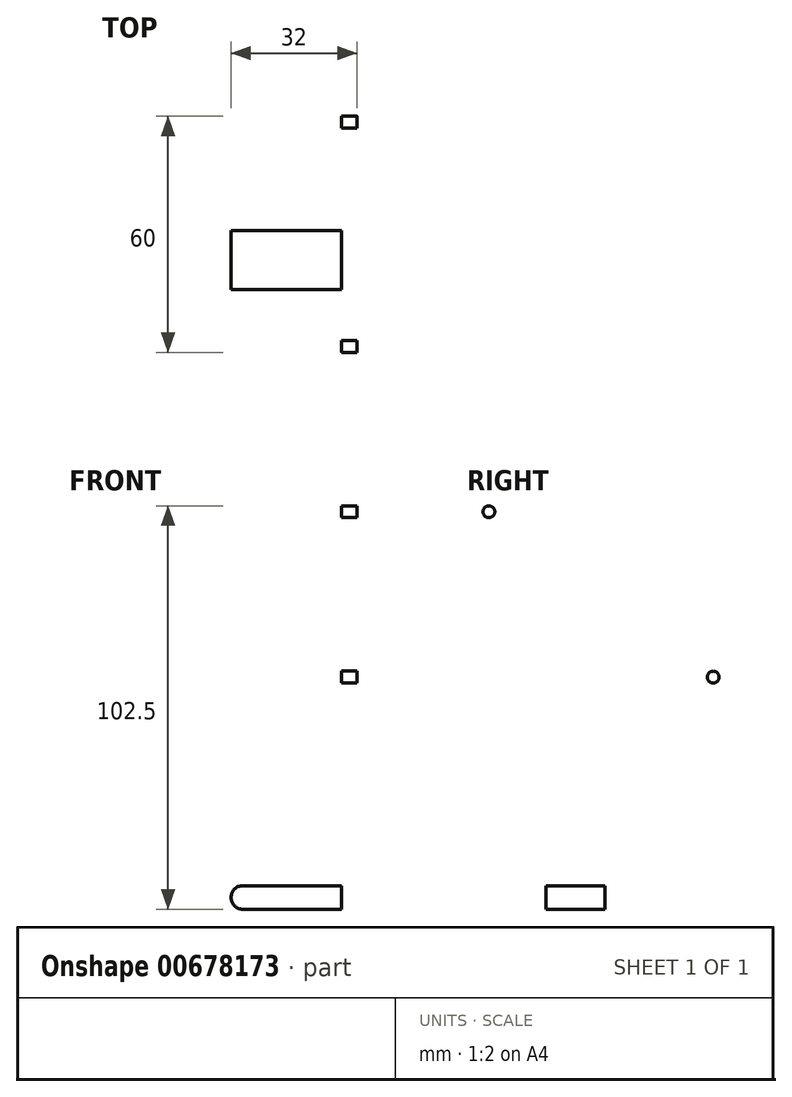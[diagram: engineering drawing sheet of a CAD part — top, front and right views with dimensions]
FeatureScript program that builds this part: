
annotation { "Feature Type Name" : "Feature", "Feature Type Description" : "" }
export const myFeature = defineFeature(function(context is Context, id is Id, definition is map)
    precondition{}
    {
        {
            var Q0;
            Q0=qCreatedBy(makeId("Right.planeOp"),FACE);
            var sketch = newSketch(context, id + "F0", { "sketchPlane" : qUnion([Q0])});
            skLineSegment(sketch, "E0.bottom", {"start": v(0, 0) * mm, "end": v(-100, 0) * mm});
            skLineSegment(sketch, "E0.top", {"start": v(0, 110) * mm, "end": v(-100, 110) * mm});
            skLineSegment(sketch, "E0.left", {"start": v(0, 0) * mm, "end": v(0, 110) * mm});
            skLineSegment(sketch, "E0.right", {"start": v(-100, 0) * mm, "end": v(-100, 110) * mm});
            skLineSegment(sketch, "E1", {"start": v(-50, 0) * mm, "end": v(-18, 0) * mm});
            skLineSegment(sketch, "E2", {"start": v(-50, 0) * mm, "end": v(-82, 0) * mm});
            skLineSegment(sketch, "E3", {"start": v(-100, 55) * mm, "end": v(-100, 65) * mm});
            skLineSegment(sketch, "E4", {"start": v(-100, 65) * mm, "end": v(-100, 45) * mm});
            skLineSegment(sketch, "E5", {"start": v(-50, 0) * mm, "end": v(-50, 110) * mm});
            skLineSegment(sketch, "E6", {"start": v(-100, 45) * mm, "end": v(-82, 0) * mm});
            skLineSegment(sketch, "E7", {"start": v(-100, 55) * mm, "end": v(0, 55) * mm});
            skLineSegment(sketch, "E8.MirrorCS", {"start": v(-100, 65) * mm, "end": v(-82, 110) * mm});
            skLineSegment(sketch, "E9.MirrorCS", {"start": v(0, 65) * mm, "end": v(-18, 110) * mm});
            skLineSegment(sketch, "E10.MirrorCS", {"start": v(0, 45) * mm, "end": v(-18, 0) * mm});
            skSolve(sketch);
        }
        {
            var Q0;
            {var subQ7=sQuery(id+"F0.wireOp",EDGE,"E9.MirrorCS");Q0=makeQuery(id+"F0.imprint","IMPRINT",FACE,{"disambiguationData":[TD([[makeQuery(id+"F0.imprint","IMPRINT",EDGE,{"derivedFrom":subQ7}),1.0]])]});}
            var Q1;
            {var subQ5=sQuery(id+"F0.wireOp",EDGE,"E1");Q1=makeQuery(id+"F0.imprint","IMPRINT",FACE,{"disambiguationData":[TD([[makeQuery(id+"F0.imprint","IMPRINT",EDGE,{"derivedFrom":subQ5}),1.0]])]});}
            var Q2;
            {var subQ7=sQuery(id+"F0.wireOp",EDGE,"E8.MirrorCS");Q2=makeQuery(id+"F0.imprint","IMPRINT",FACE,{"disambiguationData":[TD([[makeQuery(id+"F0.imprint","IMPRINT",EDGE,{"derivedFrom":subQ7}),-1.0]])]});}
            var Q3;
            {var subQ1=sQuery(id+"F0.wireOp",EDGE,"E2");Q3=makeQuery(id+"F0.imprint","IMPRINT",FACE,{"disambiguationData":[TD([[makeQuery(id+"F0.imprint","IMPRINT",EDGE,{"derivedFrom":subQ1}),-1.0]])]});}
            extrude(context, id + "F1", {"entities" : qUnion([Q0, Q1, Q2, Q3]), "depth" : 4 * mm, "offsetDistance" : 25 * mm});
        }
        {
            var Q0;
            Q0=makeQuery(id+"F1.opExtrude","CAP_FACE",FACE,{"disambiguationData":[OSD([sQuery(id+"F0.wireOp",EDGE,"E0.top"),sQuery(id+"F0.wireOp",EDGE,"E0.left"),sQuery(id+"F0.wireOp",EDGE,"E1"),sQuery(id+"F0.wireOp",EDGE,"E2"),sQuery(id+"F0.wireOp",EDGE,"E4"),sQuery(id+"F0.wireOp",EDGE,"E6"),sQuery(id+"F0.wireOp",EDGE,"E8.MirrorCS"),sQuery(id+"F0.wireOp",EDGE,"E9.MirrorCS"),sQuery(id+"F0.wireOp",EDGE,"E10.MirrorCS")])],"isStart":true});
            var sketch = newSketch(context, id + "F2", { "sketchPlane" : qUnion([Q0])});
            skLineSegment(sketch, "E11", {"start": v(50, 0) * mm, "end": v(50, 10) * mm});
            skLineSegment(sketch, "E12.bottom", {"start": v(50, 10) * mm, "end": v(57.5, 10) * mm});
            skLineSegment(sketch, "E12.top", {"start": v(50, 4) * mm, "end": v(57.5, 4) * mm});
            skLineSegment(sketch, "E12.left", {"start": v(50, 10) * mm, "end": v(50, 4) * mm});
            skLineSegment(sketch, "E12.right", {"start": v(57.5, 10) * mm, "end": v(57.5, 4) * mm});
            skLineSegment(sketch, "E13.MirrorCS", {"start": v(50, 4) * mm, "end": v(42.5, 4) * mm});
            skLineSegment(sketch, "E14.MirrorCS", {"start": v(42.5, 10) * mm, "end": v(42.5, 4) * mm});
            skLineSegment(sketch, "E15.MirrorCS", {"start": v(50, 10) * mm, "end": v(42.5, 10) * mm});
            skLineSegment(sketch, "E16", {"start": v(42.5, 7) * mm, "end": v(36.5, 7) * mm});
            skCircle(sketch, "E17", {"center": v(36.5, 7) * mm, "radius": 1.5 * mm});
            skCircle(sketch, "E18.MirrorC", {"center": v(63.5, 7) * mm, "radius": 1.5 * mm});
            skLineSegment(sketch, "E19", {"start": v(0, 45) * mm, "end": v(0, 47) * mm});
            skLineSegment(sketch, "E20", {"start": v(0, 47) * mm, "end": v(15, 47) * mm});
            skLineSegment(sketch, "E21", {"start": v(0, 55) * mm, "end": v(100, 55) * mm});
            skCircle(sketch, "E22", {"center": v(15, 47) * mm, "radius": 1.5 * mm});
            skLineSegment(sketch, "E23", {"start": v(50, 0) * mm, "end": v(50, 110) * mm});
            skCircle(sketch, "E24.MirrorC", {"center": v(15, 63) * mm, "radius": 1.5 * mm});
            skCircle(sketch, "E25.MirrorC", {"center": v(85, 63) * mm, "radius": 1.5 * mm});
            skCircle(sketch, "E26.MirrorC", {"center": v(85, 47) * mm, "radius": 1.5 * mm});
            skLineSegment(sketch, "E27", {"start": v(18, 110) * mm, "end": v(28, 110) * mm});
            skLineSegment(sketch, "E28", {"start": v(28, 110) * mm, "end": v(28, 105) * mm});
            skCircle(sketch, "E29", {"center": v(28, 105) * mm, "radius": 1.5 * mm});
            skCircle(sketch, "E30.MirrorC", {"center": v(72, 105) * mm, "radius": 1.5 * mm});
            skSolve(sketch);
        }
        {
            var Q0;
            {var subQ0=sQuery(id+"F2.wireOp",EDGE,"E12.bottom");Q0=makeQuery(id+"F2.imprint","IMPRINT",FACE,{"disambiguationData":[TD([[makeQuery(id+"F2.imprint","IMPRINT",EDGE,{"derivedFrom":subQ0}),-1.0]])]});}
            var Q1;
            {var subQ2=sQuery(id+"F2.wireOp",EDGE,"E13.MirrorCS");Q1=makeQuery(id+"F2.imprint","IMPRINT",FACE,{"disambiguationData":[TD([[makeQuery(id+"F2.imprint","IMPRINT",EDGE,{"derivedFrom":subQ2}),-1.0]])]});}
            extrude(context, id + "F3", {"entities" : qUnion([Q0, Q1]), "operationType" : NewBodyOperationType.ADD, "depth" : 28 * mm, "offsetDistance" : 25 * mm});
        }
        {
            var Q0;
            Q0=makeQuery(id+"F3.opExtrude","CAP_EDGE",EDGE,{"disambiguationData":[OSD([sQuery(id+"F2.wireOp",EDGE,"E12.top"),sQuery(id+"F2.wireOp",EDGE,"E13.MirrorCS")])],"isStart":false});
            var Q1;
            Q1=makeQuery(id+"F3.opExtrude","CAP_EDGE",EDGE,{"disambiguationData":[OSD([sQuery(id+"F2.wireOp",EDGE,"E12.bottom"),sQuery(id+"F2.wireOp",EDGE,"E15.MirrorCS")])],"isStart":false});
            fillet(context, id + "F4", {"entities" : qUnion([Q0, Q1]), "radius" : 3 * mm, "tangentPropagation" : true, "allowEdgeOverflow" : false});
        }
        {
            var Q0;
            Q0=makeQuery(id+"F2.imprint","IMPRINT",FACE,{"disambiguationData":[TD([[makeQuery(id+"F2.imprint","IMPRINT",EDGE,{"derivedFrom":sQuery(id+"F2.wireOp",EDGE,"E30.MirrorC")}),-1.0]])]});
            var Q1;
            Q1=makeQuery(id+"F2.imprint","IMPRINT",FACE,{"disambiguationData":[TD([[makeQuery(id+"F2.imprint","IMPRINT",EDGE,{"derivedFrom":sQuery(id+"F2.wireOp",EDGE,"E25.MirrorC")}),1.0]])]});
            var Q2;
            Q2=makeQuery(id+"F2.imprint","IMPRINT",FACE,{"disambiguationData":[TD([[makeQuery(id+"F2.imprint","IMPRINT",EDGE,{"derivedFrom":sQuery(id+"F2.wireOp",EDGE,"E26.MirrorC")}),-1.0]])]});
            var Q3;
            Q3=makeQuery(id+"F2.imprint","IMPRINT",FACE,{"disambiguationData":[TD([[makeQuery(id+"F2.imprint","IMPRINT",EDGE,{"derivedFrom":sQuery(id+"F2.wireOp",EDGE,"E24.MirrorC")}),-1.0]])]});
            var Q4;
            Q4=makeQuery(id+"F2.imprint","IMPRINT",FACE,{"disambiguationData":[TD([[makeQuery(id+"F2.imprint","IMPRINT",EDGE,{"derivedFrom":sQuery(id+"F2.wireOp",EDGE,"E22")}),1.0]])]});
            var Q5;
            Q5=makeQuery(id+"F2.imprint","IMPRINT",FACE,{"disambiguationData":[TD([[makeQuery(id+"F2.imprint","IMPRINT",EDGE,{"derivedFrom":sQuery(id+"F2.wireOp",EDGE,"E29")}),1.0]])]});
            var Q6;
            Q6=makeQuery(id+"F2.imprint","IMPRINT",FACE,{"disambiguationData":[TD([[makeQuery(id+"F2.imprint","IMPRINT",EDGE,{"derivedFrom":sQuery(id+"F2.wireOp",EDGE,"E18.MirrorC")}),-1.0]])]});
            var Q7;
            Q7=makeQuery(id+"F2.imprint","IMPRINT",FACE,{"disambiguationData":[TD([[makeQuery(id+"F2.imprint","IMPRINT",EDGE,{"derivedFrom":sQuery(id+"F2.wireOp",EDGE,"E17")}),1.0]])]});
            extrude(context, id + "F5", {"entities" : qUnion([Q0, Q1, Q2, Q3, Q4, Q5, Q6, Q7]), "operationType" : NewBodyOperationType.REMOVE, "oppositeDirection" : true, "depth" : 25 * mm, "offsetDistance" : 25 * mm});
        }
    });
